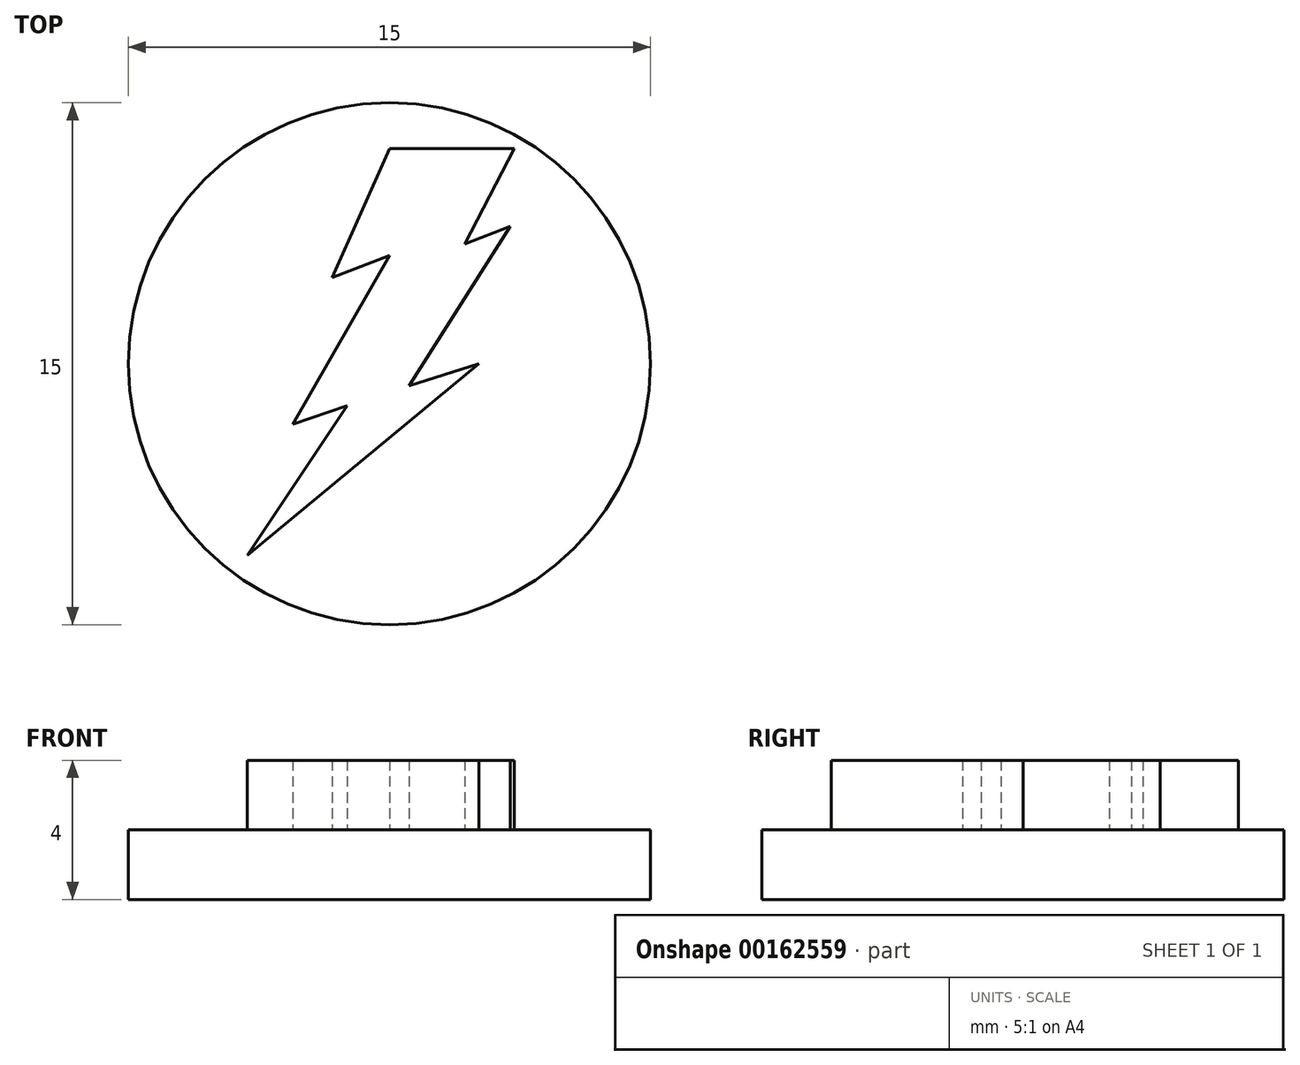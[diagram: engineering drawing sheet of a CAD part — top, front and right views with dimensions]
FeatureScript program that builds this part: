
annotation { "Feature Type Name" : "Feature", "Feature Type Description" : "" }
export const myFeature = defineFeature(function(context is Context, id is Id, definition is map)
    precondition{}
    {
        {
            var Q0;
            Q0=qCreatedBy(makeId("Top.planeOp"),FACE);
            var sketch = newSketch(context, id + "F0", { "sketchPlane" : qUnion([Q0])});
            skCircle(sketch, "E0", {"center": v(0, 0) * mm, "radius": 7.5 * mm});
            skSolve(sketch);
        }
        {
            var Q0;
            Q0 = qSketchRegion(id + "F0", true);
            extrude(context, id + "F1", {"entities" : qUnion([Q0]), "depth" : 2 * mm});
        }
        {
            var Q0;
            Q0=makeQuery(id+"F1.opExtrude","CAP_FACE",FACE,{"disambiguationData":[OSD([sQuery(id+"F0.wireOp",EDGE,"E0")])],"isStart":false});
            var sketch = newSketch(context, id + "F2", { "sketchPlane" : qUnion([Q0])});
            skLineSegment(sketch, "E1", {"start": v(0, 6.18) * mm, "end": v(-1.65, 2.47) * mm});
            skLineSegment(sketch, "E2", {"start": v(-1.65, 2.47) * mm, "end": v(0, 3.1) * mm});
            skLineSegment(sketch, "E3", {"start": v(0, 3.1) * mm, "end": v(-2.78, -1.74) * mm});
            skLineSegment(sketch, "E4", {"start": v(-2.78, -1.74) * mm, "end": v(-1.21, -1.2) * mm});
            skLineSegment(sketch, "E5", {"start": v(-1.21, -1.2) * mm, "end": v(-4.08, -5.51) * mm});
            skLineSegment(sketch, "E6", {"start": v(-4.08, -5.51) * mm, "end": v(2.57, 0) * mm});
            skLineSegment(sketch, "E7", {"start": v(2.57, 0) * mm, "end": v(0.56, -0.63) * mm});
            skLineSegment(sketch, "E8", {"start": v(0.56, -0.63) * mm, "end": v(3.47, 3.94) * mm});
            skLineSegment(sketch, "E9", {"start": v(3.47, 3.94) * mm, "end": v(2.16, 3.44) * mm});
            skLineSegment(sketch, "E10", {"start": v(2.16, 3.44) * mm, "end": v(3.58, 6.19) * mm});
            skLineSegment(sketch, "E11", {"start": v(3.58, 6.19) * mm, "end": v(0, 6.18) * mm});
            skSolve(sketch);
        }
        {
            var Q0;
            Q0 = qSketchRegion(id + "F2", true);
            extrude(context, id + "F3", {"entities" : qUnion([Q0]), "operationType" : NewBodyOperationType.ADD, "depth" : 2 * mm});
        }
    });
